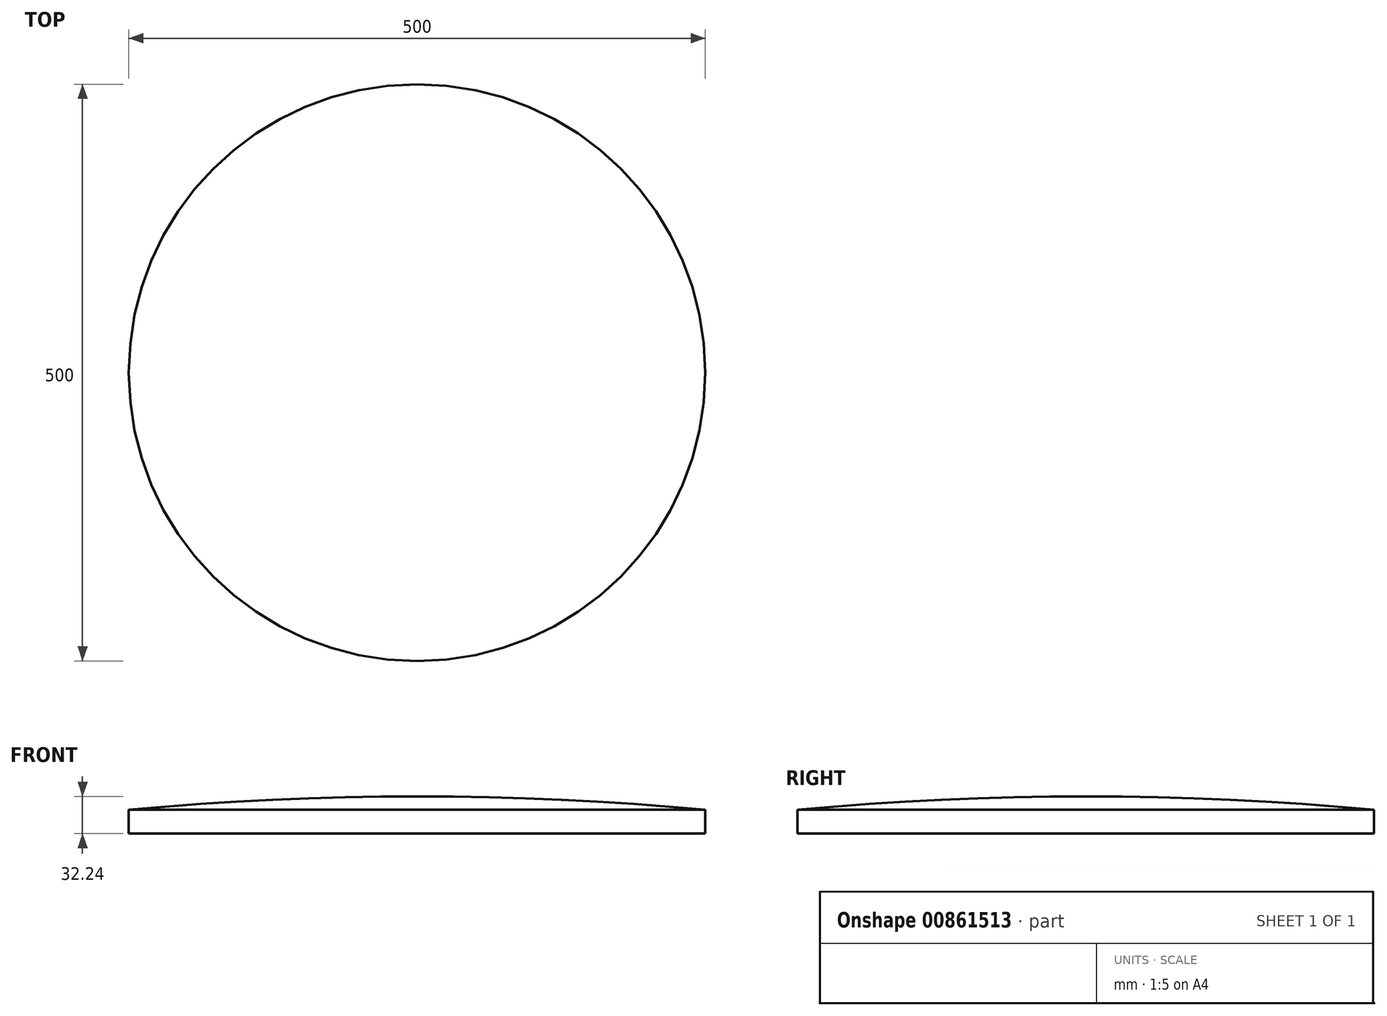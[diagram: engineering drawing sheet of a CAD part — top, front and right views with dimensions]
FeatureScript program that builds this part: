
annotation { "Feature Type Name" : "Feature", "Feature Type Description" : "" }
export const myFeature = defineFeature(function(context is Context, id is Id, definition is map)
    precondition{}
    {
        {
            var Q0;
            Q0=qCreatedBy(makeId("Top.planeOp"),FACE);
            var sketch = newSketch(context, id + "F0", { "sketchPlane" : qUnion([Q0])});
            skCircle(sketch, "E0", {"center": v(0, 0) * mm, "radius": 2700 * mm});
            skLineSegment(sketch, "E1", {"start": v(0, 0) * mm, "end": v(0, 2700) * mm});
            skLineSegment(sketch, "E2", {"start": v(0, 2700) * mm, "end": v(0, -2700) * mm});
            skSolve(sketch);
        }
        {
            var Q0;
            {var subQ0=sQuery(id+"F0.wireOp",EDGE,"E1");Q0=makeQuery(id+"F0.imprint","IMPRINT",FACE,{"disambiguationData":[TD([[makeQuery(id+"F0.imprint","IMPRINT",EDGE,{"derivedFrom":subQ0}),1.0]])]});}
            var Q1;
            Q1=sQuery(id+"F0.wireOp",EDGE,"E2");
            revolve(context, id + "F1", {"surfaceOperationType" : NewSurfaceOperationType.NEW, "entities" : qUnion([Q0]), "axis" : qUnion([Q1]), "revolveType" : RevolveType.ONE_DIRECTION, "oppositeDirection" : true, "angle" : 180 * degree});
        }
        {
            var Q0;
            Q0=qCreatedBy(makeId("Front.planeOp"),FACE);
            var sketch = newSketch(context, id + "F2", { "sketchPlane" : qUnion([Q0])});
            skLineSegment(sketch, "E3.bottom", {"start": v(-250, 0) * mm, "end": v(250, 0) * mm});
            skLineSegment(sketch, "E4.bottom", {"start": v(-250, 2667.76) * mm, "end": v(250, 2667.76) * mm});
            skLineSegment(sketch, "E4.top", {"start": v(-250, 2700) * mm, "end": v(250, 2700) * mm});
            skLineSegment(sketch, "E4.left", {"start": v(-250, 2667.76) * mm, "end": v(-250, 2700) * mm});
            skLineSegment(sketch, "E4.right", {"start": v(250, 2667.76) * mm, "end": v(250, 2700) * mm});
            skLineSegment(sketch, "E5", {"start": v(0, 0) * mm, "end": v(0, 376.88) * mm});
            skLineSegment(sketch, "E6", {"start": v(0, 2700) * mm, "end": v(0, 2667.76) * mm});
            skPoint(sketch, "E7", {"position": v(-250, 2809.06) * mm});
            skPoint(sketch, "E8", {"position": v(-250, 2687.76) * mm});
            skSolve(sketch);
        }
        {
            var Q0;
            {var subQ2=sQuery(id+"F2.wireOp",EDGE,"E4.left");Q0=makeQuery(id+"F2.imprint","IMPRINT",FACE,{"disambiguationData":[TD([[makeQuery(id+"F2.imprint","IMPRINT",EDGE,{"derivedFrom":subQ2}),-1.0]])]});}
            var Q1;
            Q1=sQuery(id+"F2.wireOp",EDGE,"E6");
            revolve(context, id + "F3", {"operationType" : NewBodyOperationType.INTERSECT, "surfaceOperationType" : NewSurfaceOperationType.NEW, "entities" : qUnion([Q0]), "axis" : qUnion([Q1]), "revolveType" : RevolveType.FULL});
        }
    });
